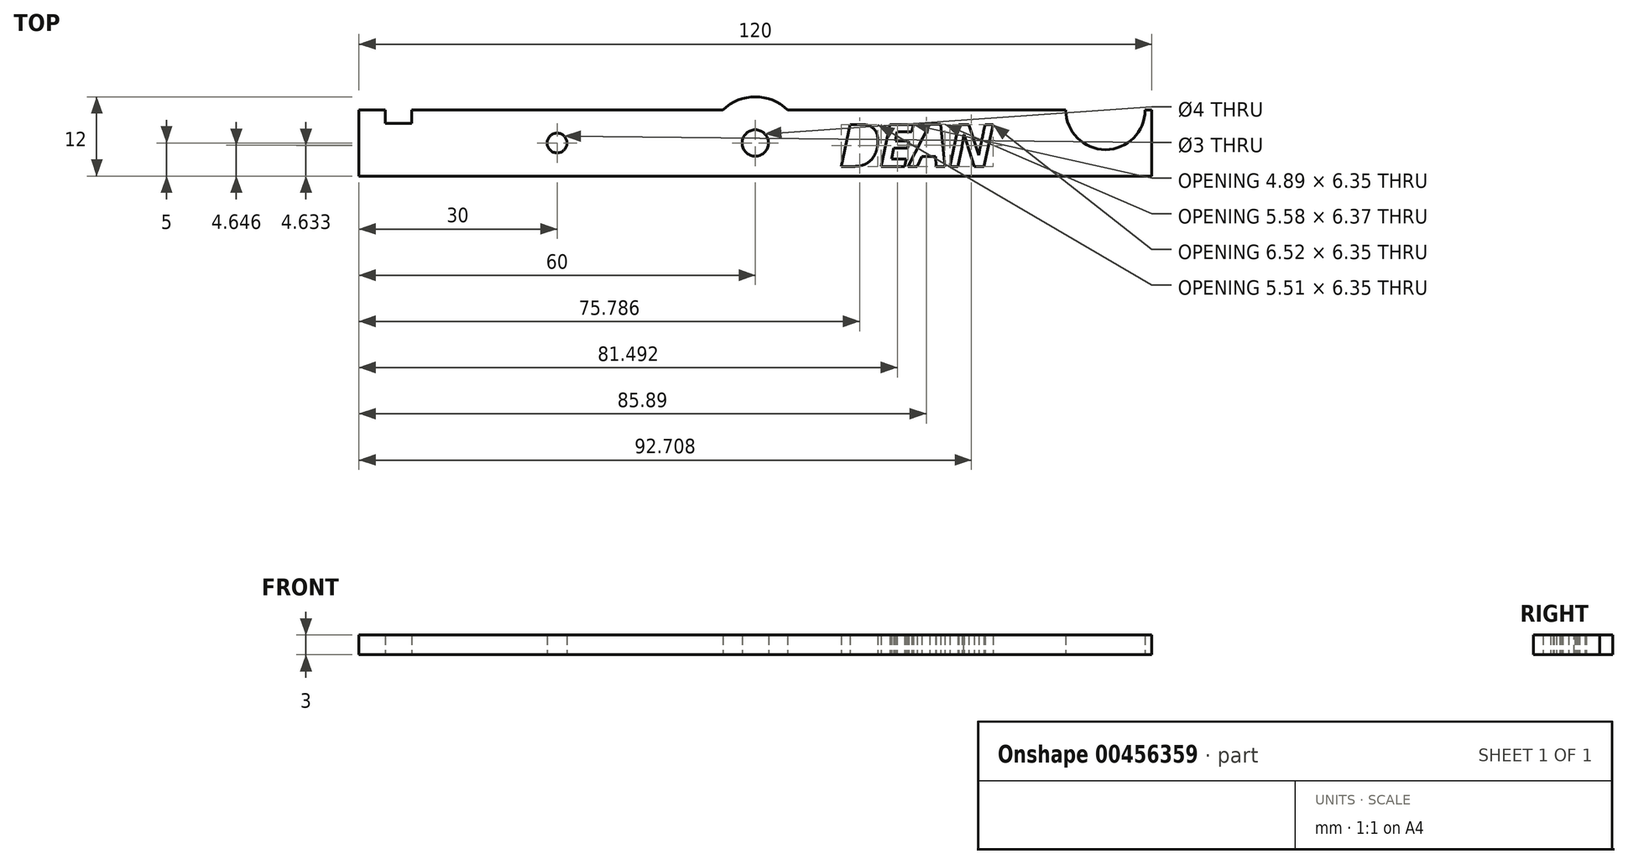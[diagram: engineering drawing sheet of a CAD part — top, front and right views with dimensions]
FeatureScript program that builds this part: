
annotation { "Feature Type Name" : "Feature", "Feature Type Description" : "" }
export const myFeature = defineFeature(function(context is Context, id is Id, definition is map)
    precondition{}
    {
        {
            var Q0;
            Q0=qCreatedBy(makeId("Top.planeOp"),FACE);
            var sketch = newSketch(context, id + "F0", { "sketchPlane" : qUnion([Q0])});
            skLineSegment(sketch, "E0.bottom", {"start": v(-60, 5) * mm, "end": v(60, 5) * mm});
            skLineSegment(sketch, "E0.top", {"start": v(-60, -5) * mm, "end": v(60, -5) * mm});
            skLineSegment(sketch, "E0.left", {"start": v(-60, 5) * mm, "end": v(-60, -5) * mm});
            skLineSegment(sketch, "E0.right", {"start": v(60, 5) * mm, "end": v(60, -5) * mm});
            skPoint(sketch, "E0.middle", {"position": v(0, 0) * mm});
            skLineSegment(sketch, "E1.bottom", {"start": v(-56, 5) * mm, "end": v(-52, 5) * mm});
            skLineSegment(sketch, "E1.top", {"start": v(-56, 3) * mm, "end": v(-52, 3) * mm});
            skLineSegment(sketch, "E1.left", {"start": v(-56, 5) * mm, "end": v(-56, 3) * mm});
            skLineSegment(sketch, "E1.right", {"start": v(-52, 5) * mm, "end": v(-52, 3) * mm});
            skCircle(sketch, "E2", {"center": v(0, 0) * mm, "radius": 2 * mm});
            skCircle(sketch, "E3", {"center": v(0, 0) * mm, "radius": 7 * mm});
            skLineSegment(sketch, "E4", {"start": v(0, 0) * mm, "end": v(-30, 0) * mm});
            skCircle(sketch, "E5", {"center": v(-30, 0) * mm, "radius": 1.5 * mm});
            skLineSegment(sketch, "E6", {"start": v(60, 5) * mm, "end": v(53, 5) * mm});
            skCircle(sketch, "E7", {"center": v(53, 5) * mm, "radius": 6 * mm});
            skText(sketch, "E8", { "text": "DEAN\n", "fontName": "OpenSans-BoldItalic.ttf"});
            const initialGuessF0  = {"E8": [0.0128, -0.00354, 1, 0, 0.0064]};
            skSetInitialGuess(sketch, initialGuessF0);
            skSolve(sketch);
        }
        {
            var Q0;
            {var subQ0=sQuery(id+"F0.wireOp",EDGE,"E0.left");Q0=makeQuery(id+"F0.imprint","IMPRINT",FACE,{"disambiguationData":[TD([[makeQuery(id+"F0.imprint","IMPRINT",EDGE,{"derivedFrom":subQ0}),1.0]])]});}
            var Q1;
            {var subQ0=sQuery(id+"F0.wireOp",EDGE,"E3");var subQ1=sQuery(id+"F0.wireOp",EDGE,"E0.bottom");var subQ2=makeQuery(id+"F0.imprint","INTERSECT",VERTEX,{"disambiguationData":[OD(0.0)],"derivedFrom":[subQ1,subQ0]});Q1=makeQuery(id+"F0.imprint","IMPRINT",FACE,{"disambiguationData":[TD([[makeQuery(id+"F0.imprint","IMPRINT",EDGE,{"disambiguationData":[TD([[subQ2,-1.0]])],"derivedFrom":subQ1}),1.0]])]});}
            var Q2;
            {var subQ0=sQuery(id+"F0.wireOp",EDGE,"E3");var subQ1=sQuery(id+"F0.wireOp",EDGE,"E0.top");var subQ2=makeQuery(id+"F0.imprint","INTERSECT",VERTEX,{"disambiguationData":[OD(0.0)],"derivedFrom":[subQ1,subQ0]});Q2=makeQuery(id+"F0.imprint","IMPRINT",FACE,{"disambiguationData":[TD([[makeQuery(id+"F0.imprint","IMPRINT",EDGE,{"disambiguationData":[TD([[subQ2,-1.0]])],"derivedFrom":subQ1}),-1.0]])]});}
            var Q3;
            Q3=makeQuery(id+"F0.imprint","IMPRINT",FACE,{"disambiguationData":[TD([[makeQuery(id+"F0.imprint","IMPRINT",EDGE,{"derivedFrom":sQuery(id+"F0.wireOp",EDGE,"E2")}),-1.0]])]});
            var Q4;
            {var subQ7=sQuery(id+"F0.wireOp",EDGE,"E0.right");Q4=makeQuery(id+"F0.imprint","IMPRINT",FACE,{"disambiguationData":[TD([[makeQuery(id+"F0.imprint","IMPRINT",EDGE,{"derivedFrom":subQ7}),-1.0]])]});}
            extrude(context, id + "F1", {"entities" : qUnion([Q0, Q1, Q2, Q3, Q4]), "depth" : 3 * mm});
        }
    });
